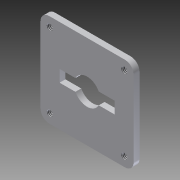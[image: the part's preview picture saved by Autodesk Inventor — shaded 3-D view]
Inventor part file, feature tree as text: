
AUTODESK INVENTOR PART (.ipt)
format: ipt  version: 2012 (Build 160160000, 160)  size: 184,832 bytes
history: native  units: in
note: dims shown in document units (in); Inventor stores cm internally (conversion verified against a paired STEP export)
features: extrude x5, fillet x3, sketch x1, hole x1
ambient origin geometry x8: Origin, YZ Plane, XZ Plane, XY Plane, X Axis, Y Axis, Z Axis, Center Point
bodies: Solid1 (feature_tree)
feature tree (10):
  sketch  "Sketch1"  dims[d0=0.9449in d1=0.4724in d2=1.0236in d3=0.5118in d4=0.0787in d5=0.2559in d6=0.128in d7=0.0787in d8=0.5625in d9=2.0in d10=1.0in d11=2.0in d12=1.0in d13=0.1181in d14=0.3937in d15=0.1575in d16=0.1575in d17=0.1575in d18=0.1575in d19=0.1575in d20=0.2in d21=0.2in d22=0.2in d23=0.2in d24=0.125in d25=0.0in d26=0.125in d34=1.6in d35=1.6in d44=0.25in d45=0.125in d46=0.0in d47=0.125in d48=0.0in d49=0.125in d50=0.0in d51=0.125in d52=0.0in d53=0.13in d54=0.75in d55=0.375in d56=0.25in d57=0.5635in d58=1.0in d59=0.8108in d60=0.1875in]
  extrude  "Extrusion1"  Depth=0.4724in
  fillet  "Fillet1"  Radius=1.0236in
  fillet  "Fillet2"  Radius=0.5118in
  extrude  "Extrusion2"  Depth=0.0787in
  extrude  "Extrusion3"  Depth=0.2559in
  extrude  "Extrusion4"  Depth=0.128in
  extrude  "Extrusion5"  Depth=0.0787in
  hole  "Hole2"  [1 undecoded]
  fillet  "Fillet3"  Radius=2.0in
note: 1 required parameter value undecoded (feature->parameter linkage not recoverable at this tier; creation-order binding heuristic only, values carry confidence <= 0.55)
